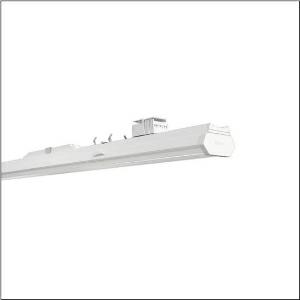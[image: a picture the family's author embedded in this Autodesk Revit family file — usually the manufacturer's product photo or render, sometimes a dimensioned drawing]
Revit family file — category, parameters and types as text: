
# Revit family: licross_r__11_protected_extreme_ho_51td1bdn4e5me_a1af
name_source: partatom
category: Lighting Fixtures
units: mm (PartAtom-declared; Revit-internal decimal feet)

## family parameters
Cut with Voids When Loaded = No
Host = Face
Light Source = No
Part Type = Normal
Room Calculation Point = No
Round Connector Dimension = Use Diameter
Shared = No

## types (1)
- --- (1 x LED, 14500 lm, 87.3 W, 4000K)
    Apparent Load = 87 VA
    CIE Flux Codes = 54 82 95 97 100
    Color Rendering = 80
    Color Temperature = 4000K
    Default Elevation = 1800 mm
    Description = Licross® 11 Protected extreme HO, luminaire insert, of sheet steel, galvanised, coil coated, white, length: 1.500mm, width: 90mm, height: 101mm, LED rated luminous flux: 14.500lm, light colour: 840, control gear: DALI 2, with plug, 5-pole, with phase selection, mains connection: 220..240V, AC, 50/60Hz, rated input power: 87W, internal wiring halogen-free, primary optical cover: cover, of PMMA, light emission: direct distribution, primary light characteristic: symmetric, protection rating (complete): IP54, insulation class (complete): insulation class I (protective earthing), certification: CE, ENEC, VDE, UKCA, protection symbol: D if used in an environment with non-conductive dust loads with corresponding accessories, impact resistance: IK06, permissible ambient temperature for indoor applications: -40..+40°C, corresponds to IFS (International Featured Standards) requirements for safety and quality in the food industry, reducing of maximum allowable ambient temperature of 5°C with ceiling mounting, LABS conformity tested according to VDMA 24364:2018-05, packaging unit: 1 piece
    Height = 92 mm
    Lamp = 1 x LED
    Lamp Light Flux = 14500 lm
    Lamp Power = 87.3 W
    Lamp count = 1
    Length = 1500 mm
    Luminous efficacy = 166 lm/W
    Manufacturer = Siteco
    ModVariant = No
    Model = 51TD1BDN4E5ME
    Mounting Place = Ceiling
    Mounting Type = Pendant
    Number of Poles = 1
    OnlyDefault = Yes
    Power Factor = 1
    Product Name = Licross® 11 Protected extreme HO
    Product group = luminaire insert | ceiling pendant
    ProductGroupID = 902
    Protection Class = Protection class I
    Protection Degree = IP 54
    RLX_Detail_Level = 1
    RLX_Emergency_Light_Flux = 0 lm
    RLX_Emergency_Type = 0
    RLX_Emergency_Type_DB = No
    RlxData = <blob elided: 24325 chars, md5=c39c2553>
    Socket = socket
    Standby Power = 0 W
    System Light Flux = 14500 lm
    System Power = 87 W
    Type Comments = factory setting: luminous flux: 100 % | dim-lin: 254 | 589 mA
    Type Image = l_1256145.jpg
    URL = http://relux.com
    VarID = @adj_104423
    Voltage = 0 V
    Weight = 0.00 kg
    Width = 88 mm

## geometry (parser evidence)
native form markers: Blend x4, Sweep x10
no freeform markers — native parametric forms only
